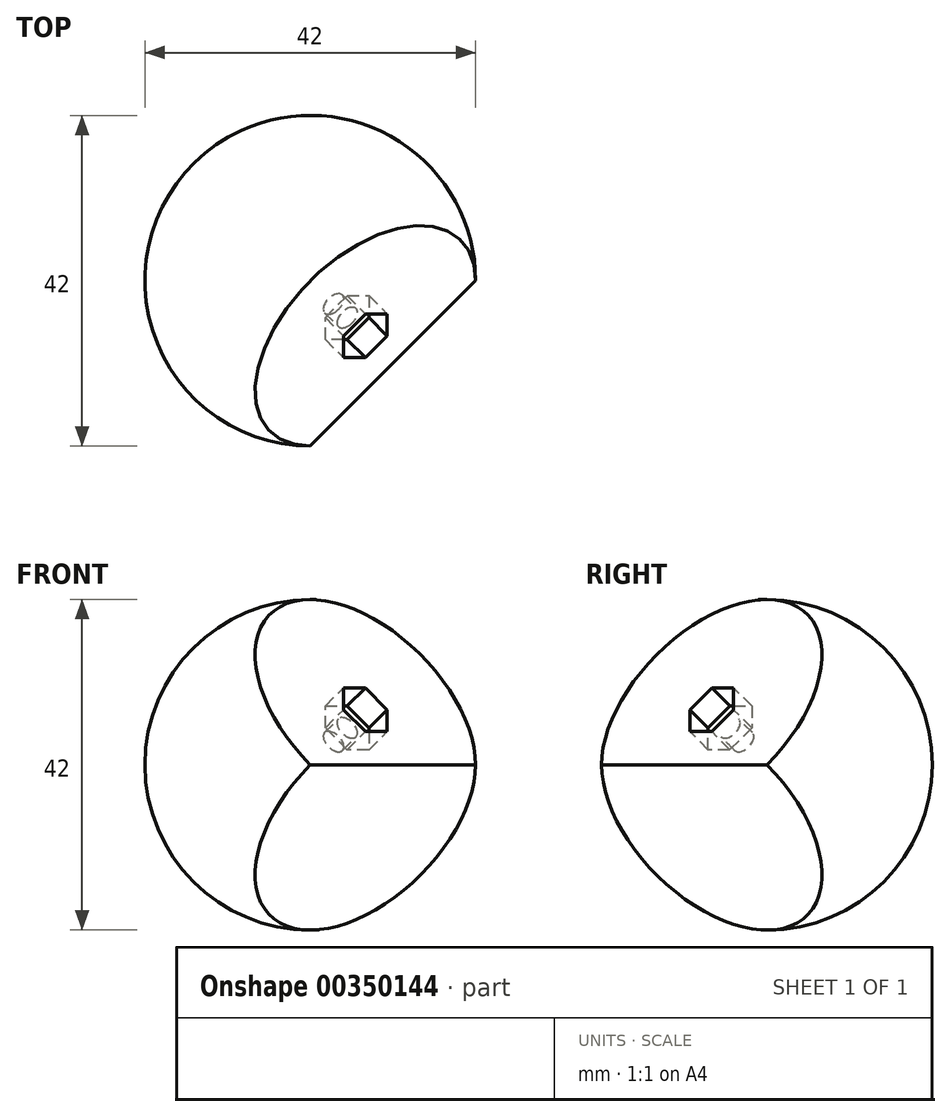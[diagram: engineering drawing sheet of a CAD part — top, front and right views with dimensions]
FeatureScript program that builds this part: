
annotation { "Feature Type Name" : "Feature", "Feature Type Description" : "" }
export const myFeature = defineFeature(function(context is Context, id is Id, definition is map)
    precondition{}
    {
        {
            var Q0;
            Q0=qCreatedBy(makeId("Front.planeOp"),FACE);
            var sketch = newSketch(context, id + "F0", { "sketchPlane" : qUnion([Q0])});
            skCircle(sketch, "E0.cCircle", {"center": v(0, 0) * mm, "radius": 14.85 * mm, "construction": true});
            skLineSegment(sketch, "E0.0", {"start": v(0, 21) * mm, "end": v(10.5, 10.5) * mm});
            skLineSegment(sketch, "E0.1", {"start": v(21, 0) * mm, "end": v(10.5, -10.5) * mm});
            skLineSegment(sketch, "E0.2", {"start": v(0, -21) * mm, "end": v(-21, 0) * mm});
            skLineSegment(sketch, "E0.3", {"start": v(-21, 0) * mm, "end": v(0, 21) * mm});
            skPoint(sketch, "E0.0.midPoint", {"position": v(10.5, 10.5) * mm});
            skLineSegment(sketch, "E1", {"start": v(0, -21) * mm, "end": v(0, 21) * mm});
            skArc(sketch, "E2", {"start": v(0, -21) * mm, "mid": v(21, 0) * mm, "end": v(0, 21) * mm});
            skLineSegment(sketch, "E3", {"start": v(0, 0) * mm, "end": v(10.5, 10.5) * mm, "construction": true});
            skLineSegment(sketch, "E4", {"start": v(0, 0) * mm, "end": v(10.5, -10.5) * mm, "construction": true});
            skLineSegment(sketch, "E5", {"start": v(10.5, 10.5) * mm, "end": v(21, 0) * mm});
            skLineSegment(sketch, "E6", {"start": v(10.5, -10.5) * mm, "end": v(0, -21) * mm});
            skLineSegment(sketch, "E7", {"start": v(10.5, 10.5) * mm, "end": v(14.85, 14.85) * mm});
            skSolve(sketch);
        }
        {
            var Q0;
            Q0=makeQuery(id+"F0.imprint","IMPRINT",FACE,{"disambiguationData":[TD([[makeQuery(id+"F0.imprint","IMPRINT",EDGE,{"derivedFrom":sQuery(id+"F0.wireOp",EDGE,"E0.0")}),-1.0]])]});
            var Q1;
            {var subQ0=sQuery(id+"F0.wireOp",EDGE,"E0.0");Q1=makeQuery(id+"F0.imprint","IMPRINT",FACE,{"disambiguationData":[TD([[makeQuery(id+"F0.imprint","IMPRINT",EDGE,{"derivedFrom":subQ0}),1.0]])]});}
            var Q2;
            {var subQ0=sQuery(id+"F0.wireOp",EDGE,"E0.1");Q2=makeQuery(id+"F0.imprint","IMPRINT",FACE,{"disambiguationData":[TD([[makeQuery(id+"F0.imprint","IMPRINT",EDGE,{"derivedFrom":subQ0}),1.0]])]});}
            var Q3;
            {var subQ0=sQuery(id+"F0.wireOp",EDGE,"E5");Q3=makeQuery(id+"F0.imprint","IMPRINT",FACE,{"disambiguationData":[TD([[makeQuery(id+"F0.imprint","IMPRINT",EDGE,{"derivedFrom":subQ0}),1.0]])]});}
            var Q4;
            Q4=sQuery(id+"F0.wireOp",EDGE,"E1");
            revolve(context, id + "F1", {"entities" : qUnion([Q0, Q1, Q2, Q3]), "axis" : qUnion([Q4]), "revolveType" : RevolveType.FULL});
        }
        {
            var Q0;
            Q0=sQuery(id+"F0.wireOp",EDGE,"E1");
            cPlane(context, id + "F2", {"entities" : qUnion([Q0]), "cplaneType" : CPlaneType.LINE_ANGLE, "offset" : 25 * mm, "angle" : 45 * degree, "width" : 150 * mm, "height" : 150 * mm});
        }
        {
            var Q0;
            Q0=qCreatedBy(id+"F2.planeOp",FACE);
            var sketch = newSketch(context, id + "F3", { "sketchPlane" : qUnion([Q0])});
            skLineSegment(sketch, "E8.0", {"start": v(-7.42, 10.5) * mm, "end": v(-14.85, 0) * mm});
            skLineSegment(sketch, "E8.1", {"start": v(0, 21) * mm, "end": v(-7.42, 10.5) * mm});
            skLineSegment(sketch, "E9.0", {"start": v(-7.42, -10.5) * mm, "end": v(0, -21) * mm});
            skLineSegment(sketch, "E10.0", {"start": v(-14.85, 0) * mm, "end": v(-7.42, -10.5) * mm});
            skLineSegment(sketch, "E11", {"start": v(0, 21) * mm, "end": v(-23.62, 21) * mm});
            skLineSegment(sketch, "E12", {"start": v(-23.62, 21) * mm, "end": v(-23.62, -21) * mm});
            skLineSegment(sketch, "E13", {"start": v(-23.62, -21) * mm, "end": v(0, -21) * mm});
            skSolve(sketch);
        }
        {
            var Q0;
            Q0=makeQuery(id+"F3.imprint","IMPRINT",FACE,{"disambiguationData":[TD([[makeQuery(id+"F3.imprint","IMPRINT",EDGE,{"derivedFrom":sQuery(id+"F3.wireOp",EDGE,"E8.0")}),-1.0]])]});
            extrude(context, id + "F4", {"entities" : qUnion([Q0]), "operationType" : NewBodyOperationType.REMOVE, "endBound" : BoundingType.THROUGH_ALL, "oppositeDirection" : true, "depth" : 25 * mm, "hasSecondDirection" : true, "secondDirectionBound" : SecondDirectionBoundingType.THROUGH_ALL, "secondDirectionOppositeDirection" : false, "secondDirectionDepth" : 25 * mm});
        }
        {
            var Q0;
            Q0=makeQuery(id+"F4.boolean.opBoolean","COPY",FACE,{"derivedFrom":makeQuery(id+"F4.opExtrude","SWEPT_FACE",FACE,{"disambiguationData":[OSD([sQuery(id+"F3.wireOp",EDGE,"E8.0"),sQuery(id+"F3.wireOp",EDGE,"E8.1")])]})});
            var sketch = newSketch(context, id + "F5", { "sketchPlane" : qUnion([Q0])});
            skPoint(sketch, "E14.0", {"position": v(0, 0) * mm});
            skCircle(sketch, "E15.cCircle", {"center": v(0, 0) * mm, "radius": 3.4 * mm, "construction": true});
            skLineSegment(sketch, "E15.0", {"start": v(3.4, 1.96) * mm, "end": v(3.4, -1.96) * mm});
            skLineSegment(sketch, "E15.1", {"start": v(3.4, -1.96) * mm, "end": v(0, -3.93) * mm});
            skLineSegment(sketch, "E15.2", {"start": v(0, -3.93) * mm, "end": v(-3.4, -1.96) * mm});
            skLineSegment(sketch, "E15.3", {"start": v(-3.4, -1.96) * mm, "end": v(-3.4, 1.96) * mm});
            skLineSegment(sketch, "E15.4", {"start": v(-3.4, 1.96) * mm, "end": v(0, 3.93) * mm});
            skLineSegment(sketch, "E15.5", {"start": v(0, 3.93) * mm, "end": v(3.4, 1.96) * mm});
            skPoint(sketch, "E15.0.midPoint", {"position": v(3.4, 0) * mm});
            skCircle(sketch, "E16", {"center": v(0, 0) * mm, "radius": 1.6 * mm});
            skSolve(sketch);
        }
        {
            var Q0;
            Q0=makeQuery(id+"F5.imprint","IMPRINT",FACE,{"disambiguationData":[TD([[makeQuery(id+"F5.imprint","IMPRINT",EDGE,{"derivedFrom":sQuery(id+"F5.wireOp",EDGE,"E15.0")}),-1.0]])]});
            var Q1;
            Q1=makeQuery(id+"F5.imprint","IMPRINT",FACE,{"disambiguationData":[TD([[makeQuery(id+"F5.imprint","IMPRINT",EDGE,{"derivedFrom":sQuery(id+"F5.wireOp",EDGE,"E16")}),1.0]])]});
            extrude(context, id + "F6", {"entities" : qUnion([Q0, Q1]), "operationType" : NewBodyOperationType.REMOVE, "oppositeDirection" : true, "depth" : 4 * mm});
        }
        {
            var Q0;
            Q0=makeQuery(id+"F5.imprint","IMPRINT",FACE,{"disambiguationData":[TD([[makeQuery(id+"F5.imprint","IMPRINT",EDGE,{"derivedFrom":sQuery(id+"F5.wireOp",EDGE,"E16")}),1.0]])]});
            extrude(context, id + "F7", {"entities" : qUnion([Q0]), "operationType" : NewBodyOperationType.REMOVE, "oppositeDirection" : true, "depth" : 7 * mm});
        }
    });
